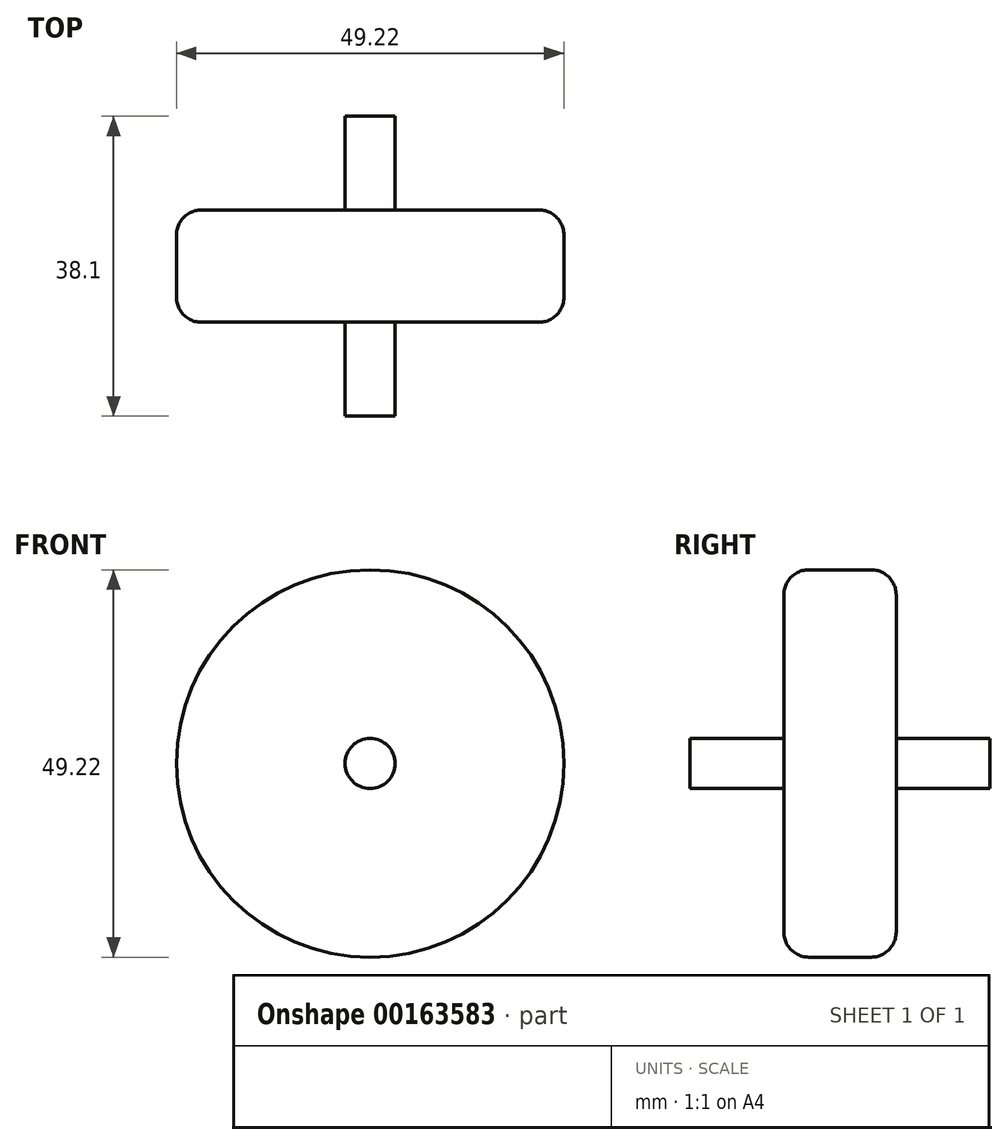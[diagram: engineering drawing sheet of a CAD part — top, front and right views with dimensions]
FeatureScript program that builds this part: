
annotation { "Feature Type Name" : "Feature", "Feature Type Description" : "" }
export const myFeature = defineFeature(function(context is Context, id is Id, definition is map)
    precondition{}
    {
        {
            var Q0;
            Q0=qCreatedBy(makeId("Front.planeOp"),FACE);
            var sketch = newSketch(context, id + "F0", { "sketchPlane" : qUnion([Q0])});
            skCircle(sketch, "E0", {"center": v(0, 0) * mm, "radius": 3.18 * mm});
            skSolve(sketch);
        }
        {
            var Q0;
            Q0 = qSketchRegion(id + "F0", true);
            extrude(context, id + "F1", {"entities" : qUnion([Q0]), "depth" : 38.1 * mm});
        }
        {
            var Q0;
            Q0=qCreatedBy(makeId("Front.planeOp"),FACE);
            var sketch = newSketch(context, id + "F2", { "sketchPlane" : qUnion([Q0])});
            skCircle(sketch, "E1", {"center": v(0, 0) * mm, "radius": 24.6 * mm});
            skSolve(sketch);
        }
        {
            var Q0;
            Q0 = qSketchRegion(id + "F2", true);
            extrude(context, id + "F3", {"entities" : qUnion([Q0]), "operationType" : NewBodyOperationType.ADD, "depth" : 26.16 * mm, "hasSecondDirection" : true, "secondDirectionOppositeDirection" : false, "secondDirectionDepth" : 11.9 * mm});
        }
        {
            var Q0;
            Q0=makeQuery(id+"F3.opExtrude","CAP_EDGE",EDGE,{"disambiguationData":[OSD([sQuery(id+"F2.wireOp",EDGE,"E1")])],"isStart":false});
            fillet(context, id + "F4", {"entities" : qUnion([Q0]), "radius" : 3.17 * mm, "tangentPropagation" : true, "allowEdgeOverflow" : false});
        }
        {
            var Q0;
            Q0=makeQuery(id+"F3.opExtrude","CAP_EDGE",EDGE,{"disambiguationData":[OSD([sQuery(id+"F2.wireOp",EDGE,"E1")])],"isStart":true});
            fillet(context, id + "F5", {"entities" : qUnion([Q0]), "radius" : 3.17 * mm, "tangentPropagation" : true, "allowEdgeOverflow" : false});
        }
    });
